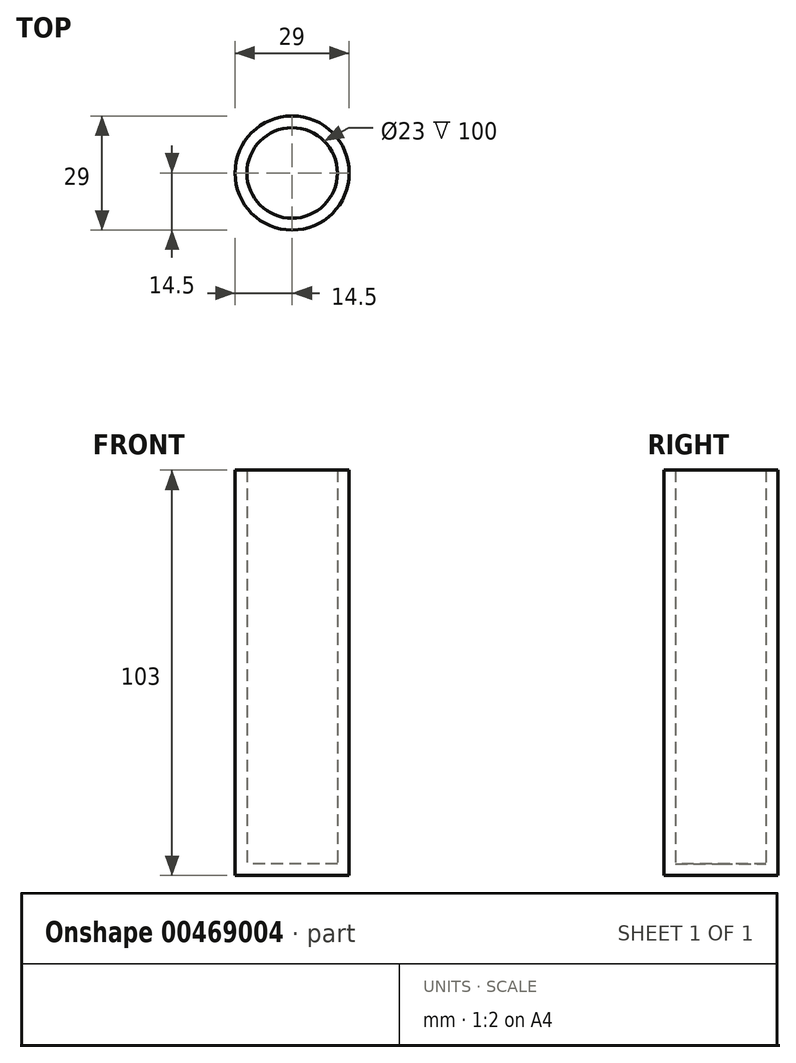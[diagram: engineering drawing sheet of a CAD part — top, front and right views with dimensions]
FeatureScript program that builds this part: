
annotation { "Feature Type Name" : "Feature", "Feature Type Description" : "" }
export const myFeature = defineFeature(function(context is Context, id is Id, definition is map)
    precondition{}
    {
        {
            assignVariable(context, id + "F0", {"name" : "longueur", "anyValue" : 100});
        }
        {
            var Q0;
            Q0=qCreatedBy(makeId("Top.planeOp"),FACE);
            var sketch = newSketch(context, id + "F1", { "sketchPlane" : qUnion([Q0])});
            skCircle(sketch, "E0", {"center": v(0, 0) * mm, "radius": 11.5 * mm});
            skCircle(sketch, "E1", {"center": v(0, 0) * mm, "radius": 14.5 * mm});
            skSolve(sketch);
        }
        {
            var Q0;
            Q0 = qSketchRegion(id + "F1", true);
            extrude(context, id + "F2", {"entities" : qUnion([Q0]), "depth" : (getVariable(context, 'longueur')) * mm});
        }
        {
            var Q0;
            Q0=qCreatedBy(makeId("Top.planeOp"),FACE);
            var sketch = newSketch(context, id + "F3", { "sketchPlane" : qUnion([Q0])});
            skCircle(sketch, "E2", {"center": v(0, 0) * mm, "radius": 14.5 * mm});
            skSolve(sketch);
        }
        {
            var Q0;
            Q0=makeQuery(id+"F3.imprint","IMPRINT",FACE,{"disambiguationData":[TD([[makeQuery(id+"F3.imprint","IMPRINT",EDGE,{"derivedFrom":sQuery(id+"F3.wireOp",EDGE,"E2")}),1.0]])]});
            extrude(context, id + "F4", {"entities" : qUnion([Q0]), "operationType" : NewBodyOperationType.ADD, "oppositeDirection" : true, "depth" : 3 * mm});
        }
    });
